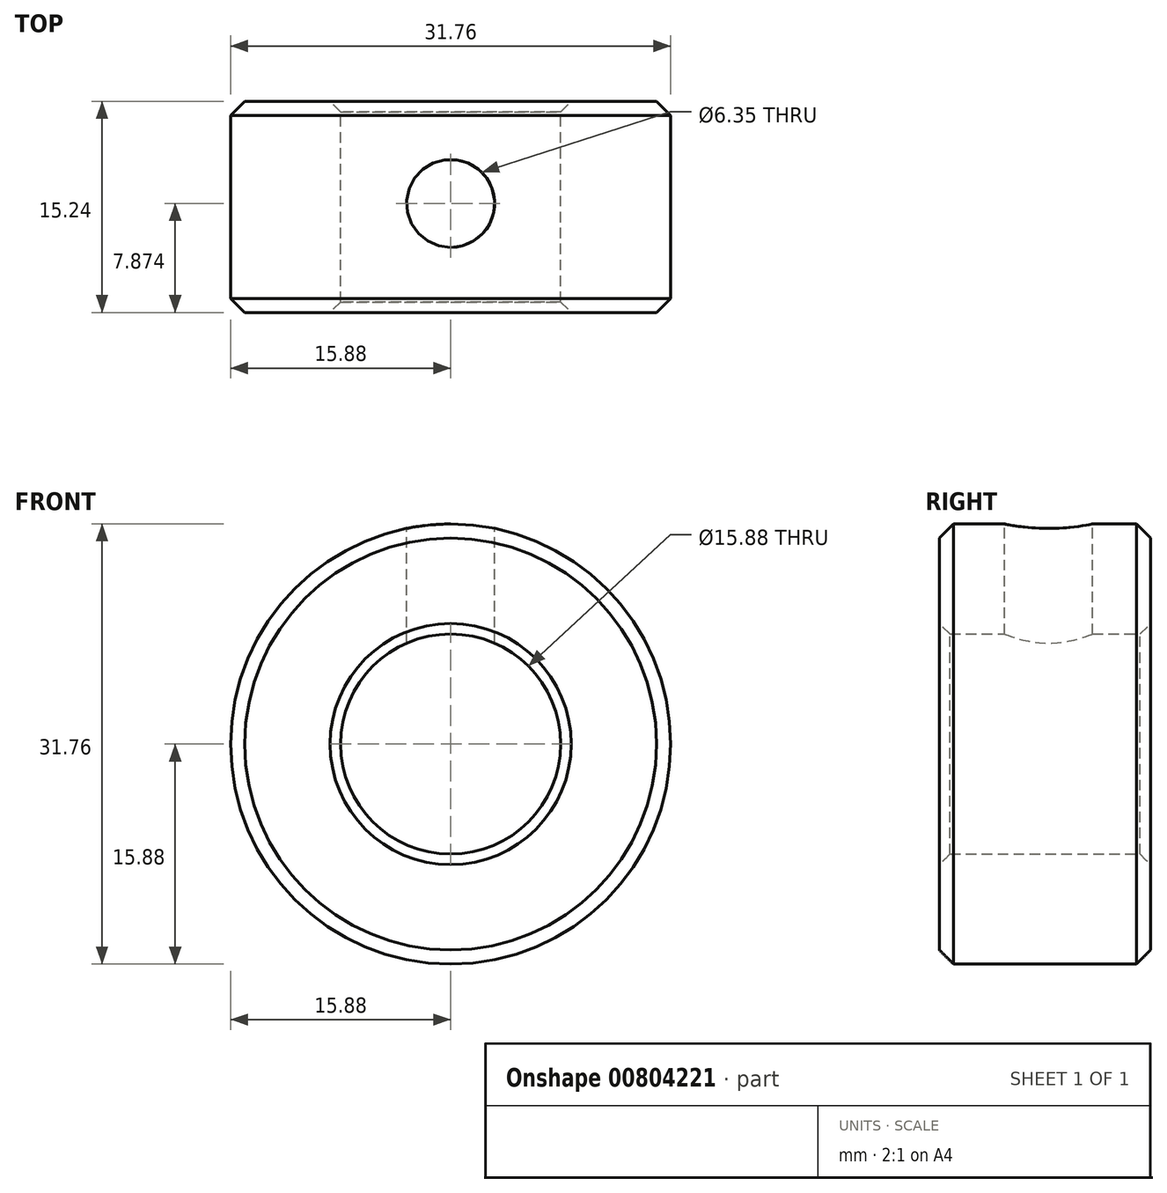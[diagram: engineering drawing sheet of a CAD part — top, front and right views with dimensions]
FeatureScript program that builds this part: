
annotation { "Feature Type Name" : "Feature", "Feature Type Description" : "" }
export const myFeature = defineFeature(function(context is Context, id is Id, definition is map)
    precondition{}
    {
        {
            var Q0;
            Q0=qCreatedBy(makeId("Front.planeOp"),FACE);
            var sketch = newSketch(context, id + "F0", { "sketchPlane" : qUnion([Q0])});
            skCircle(sketch, "E0", {"center": v(0, 0) * mm, "radius": 15.88 * mm});
            skCircle(sketch, "E1", {"center": v(0, 0) * mm, "radius": 7.94 * mm});
            skSolve(sketch);
        }
        {
            var Q0;
            Q0=makeQuery(id+"F0.imprint","IMPRINT",FACE,{"disambiguationData":[TD([[makeQuery(id+"F0.imprint","IMPRINT",EDGE,{"derivedFrom":sQuery(id+"F0.wireOp",EDGE,"E0")}),1.0]])]});
            extrude(context, id + "F1", {"entities" : qUnion([Q0]), "depth" : 15.24 * mm, "offsetDistance" : 25.4 * mm});
        }
        {
            var Q0;
            Q0=makeQuery(id+"F1.opExtrude","CAP_EDGE",EDGE,{"disambiguationData":[OSD([sQuery(id+"F0.wireOp",EDGE,"E0")])],"isStart":false});
            var Q1;
            Q1=makeQuery(id+"F1.opExtrude","CAP_EDGE",EDGE,{"disambiguationData":[OSD([sQuery(id+"F0.wireOp",EDGE,"E0")])],"isStart":true});
            chamfer(context, id + "F2", {"entities" : qUnion([Q0, Q1]), "width" : 1.02 * mm, "tangentPropagation" : true});
        }
        {
            var Q0;
            Q0=makeQuery(id+"F1.opExtrude","CAP_EDGE",EDGE,{"disambiguationData":[OSD([sQuery(id+"F0.wireOp",EDGE,"E1")])],"isStart":false});
            var Q1;
            Q1=makeQuery(id+"F1.opExtrude","CAP_EDGE",EDGE,{"disambiguationData":[OSD([sQuery(id+"F0.wireOp",EDGE,"E1")])],"isStart":true});
            chamfer(context, id + "F3", {"entities" : qUnion([Q0, Q1]), "width" : 0.76 * mm, "tangentPropagation" : true});
        }
        {
            var Q0;
            Q0=qCreatedBy(makeId("Top.planeOp"),FACE);
            cPlane(context, id + "F4", {"entities" : qUnion([Q0]), "cplaneType" : CPlaneType.OFFSET, "offset" : 15.88 * mm, "width" : 152.4 * mm, "height" : 152.4 * mm});
        }
        {
            var Q0;
            Q0=qCreatedBy(id+"F4.planeOp",FACE);
            var sketch = newSketch(context, id + "F5", { "sketchPlane" : qUnion([Q0])});
            skCircle(sketch, "E2", {"center": v(0, -7.37) * mm, "radius": 3.18 * mm});
            skSolve(sketch);
        }
        {
            var Q0;
            Q0=makeQuery(id+"F5.imprint","IMPRINT",FACE,{"disambiguationData":[TD([[makeQuery(id+"F5.imprint","IMPRINT",EDGE,{"derivedFrom":sQuery(id+"F5.wireOp",EDGE,"E2")}),1.0]])]});
            extrude(context, id + "F6", {"entities" : qUnion([Q0]), "operationType" : NewBodyOperationType.REMOVE, "oppositeDirection" : true, "depth" : 14.22 * mm, "offsetDistance" : 25.4 * mm});
        }
    });
